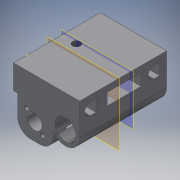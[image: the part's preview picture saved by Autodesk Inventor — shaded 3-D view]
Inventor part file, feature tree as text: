
AUTODESK INVENTOR PART (.ipt)
format: ipt  version: 2016 (Build 200138000, 138)  size: 1,509,888 bytes
history: native  units: mm
features: sketch x7, projected_geometry x5, extrude x4, other x3, hole x2, plane x2, direct_edit x1, move_body x1
ambient origin geometry x8: Origin, YZ Plane, XZ Plane, XY Plane, X Axis, Y Axis, Z Axis, Center Point
bodies: Solid1 (feature_tree)
feature tree (25):
  other  "z_right_printer_1"
  other  "MeshFeature1"
  direct_edit  "Direct Edit1"
  sketch  "Sketch1"  dims[d0=0.0mm d1=0.0mm d2=5.5mm]
  other  "Work Point1"
  hole  "Hole1"  [1 undecoded]
  extrude  "Extrusion1"  Depth=16.0mm
  hole  "Hole2"  [1 undecoded]
  sketch  "Sketch5"  dims[d14=3.2mm d15=6.0mm d16=4.0mm d17=2.0mm d18=90.0deg d19=23.5mm d20=20.594885mm d21=1.0mm]
  extrude  "Extrusion2"  Depth=1.0mm TaperAngle=0.0deg
  extrude  "Extrusion3"  [1 undecoded]
  plane  "Work Plane1"
  plane  "Work Plane2"
  extrude  "Extrusion4"  [1 undecoded]
  projected_geometry  "Projected Loop1"
  sketch  "Sketch3"  dims[d3=10.8mm d4=6.0mm d5=4.0mm d6=2.0mm d7=90.0deg d8=8.0mm d9=20.594885mm d10=16.0mm]
  projected_geometry  "Projected Loop3"
  sketch  "Sketch4"  dims[d11=10.0mm d12=0.0mm d13=16.0mm]
  sketch  "Sketch6"  dims[d22=1.0mm d23=0.0mm d24=1.0mm d25=0.0mm]
  sketch  "Sketch7"  dims[d26=-26.0mm d27=-26.0mm]
  projected_geometry  "Projected Loop5"
  projected_geometry  "Projected Loop6"
  sketch  "Sketch8"  dims[d28=7.5mm d29=0.0mm]
  projected_geometry  "Projected Loop7"
  move_body  "Move1"
note: 4 required parameter values undecoded (feature->parameter linkage not recoverable at this tier; creation-order binding heuristic only, values carry confidence <= 0.55)
